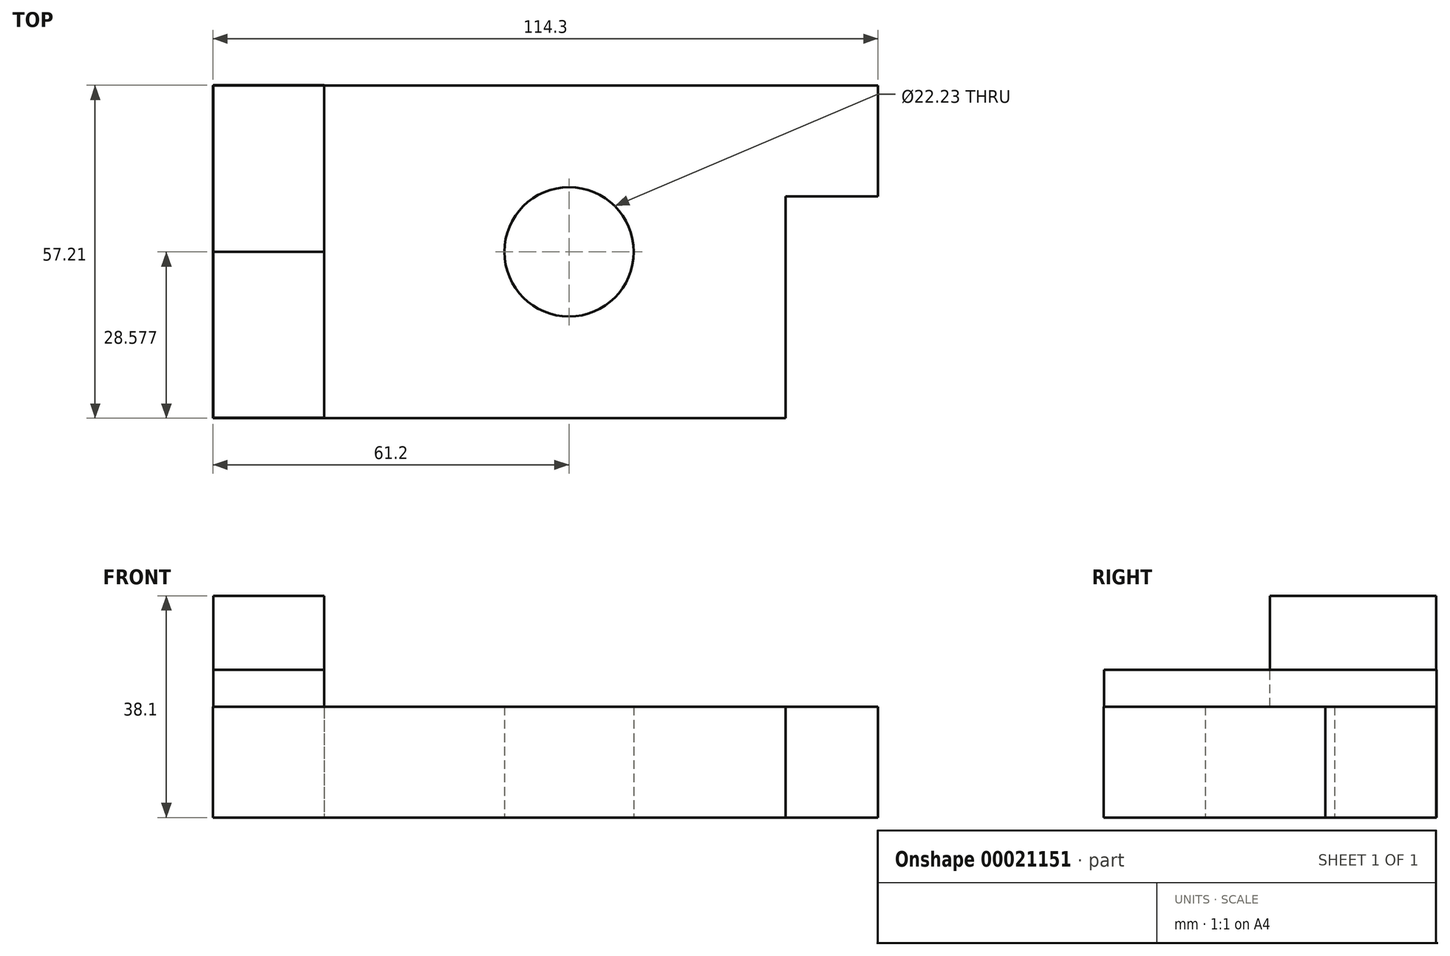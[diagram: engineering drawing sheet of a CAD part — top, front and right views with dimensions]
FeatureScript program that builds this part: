
annotation { "Feature Type Name" : "Feature", "Feature Type Description" : "" }
export const myFeature = defineFeature(function(context is Context, id is Id, definition is map)
    precondition{}
    {
        {
            var Q0;
            Q0=qCreatedBy(makeId("Top.planeOp"),FACE);
            var sketch = newSketch(context, id + "F0", { "sketchPlane" : qUnion([Q0])});
            skLineSegment(sketch, "E0.bottom", {"start": v(-56.25, 18) * mm, "end": v(58.05, 18) * mm});
            skLineSegment(sketch, "E0.top", {"start": v(-56.25, -39.16) * mm, "end": v(58.05, -39.16) * mm});
            skLineSegment(sketch, "E0.left", {"start": v(-56.25, 18) * mm, "end": v(-56.25, -39.16) * mm});
            skLineSegment(sketch, "E0.right", {"start": v(58.05, 18) * mm, "end": v(58.05, -39.16) * mm});
            skLineSegment(sketch, "E1.bottom", {"start": v(42.18, -1.06) * mm, "end": v(58.05, -1.06) * mm});
            skLineSegment(sketch, "E1.top", {"start": v(42.18, -39.16) * mm, "end": v(58.05, -39.16) * mm});
            skLineSegment(sketch, "E1.left", {"start": v(42.18, -1.06) * mm, "end": v(42.18, -39.16) * mm});
            skLineSegment(sketch, "E1.right", {"start": v(58.05, -1.06) * mm, "end": v(58.05, -39.16) * mm});
            skCircle(sketch, "E2", {"center": v(4.95, -10.58) * mm, "radius": 11.11 * mm});
            skSolve(sketch);
        }
        {
            var Q0;
            Q0=makeQuery(id+"F0.imprint","IMPRINT",FACE,{"disambiguationData":[TD([[makeQuery(id+"F0.imprint","IMPRINT",EDGE,{"derivedFrom":sQuery(id+"F0.wireOp",EDGE,"E0.bottom")}),-1.0]])]});
            extrude(context, id + "F1", {"entities" : qUnion([Q0]), "depth" : 19.05 * mm});
        }
        {
            var Q0;
            Q0=qCreatedBy(makeId("Top.planeOp"),FACE);
            var sketch = newSketch(context, id + "F2", { "sketchPlane" : qUnion([Q0])});
            skLineSegment(sketch, "E3.bottom", {"start": v(-56.19, 18.05) * mm, "end": v(-37.14, 18.05) * mm});
            skLineSegment(sketch, "E3.top", {"start": v(-56.19, -39.1) * mm, "end": v(-37.14, -39.1) * mm});
            skLineSegment(sketch, "E3.left", {"start": v(-56.19, 18.05) * mm, "end": v(-56.19, -39.1) * mm});
            skLineSegment(sketch, "E3.right", {"start": v(-37.14, 18.05) * mm, "end": v(-37.14, -39.1) * mm});
            skSolve(sketch);
        }
        {
            var Q0;
            Q0 = qSketchRegion(id + "F2", true);
            extrude(context, id + "F3", {"entities" : qUnion([Q0]), "operationType" : NewBodyOperationType.ADD, "depth" : 25.4 * mm});
        }
        {
            var Q0;
            Q0=qCreatedBy(makeId("Top.planeOp"),FACE);
            var sketch = newSketch(context, id + "F4", { "sketchPlane" : qUnion([Q0])});
            skLineSegment(sketch, "E4.bottom", {"start": v(-56.2, 17.99) * mm, "end": v(-37.16, 17.99) * mm});
            skLineSegment(sketch, "E4.top", {"start": v(-56.2, -10.59) * mm, "end": v(-37.16, -10.59) * mm});
            skLineSegment(sketch, "E4.left", {"start": v(-56.2, 17.99) * mm, "end": v(-56.2, -10.59) * mm});
            skLineSegment(sketch, "E4.right", {"start": v(-37.16, 17.99) * mm, "end": v(-37.16, -10.59) * mm});
            skSolve(sketch);
        }
        {
            var Q0;
            Q0 = qSketchRegion(id + "F4", true);
            extrude(context, id + "F5", {"entities" : qUnion([Q0]), "operationType" : NewBodyOperationType.ADD, "depth" : 38.1 * mm});
        }
    });
